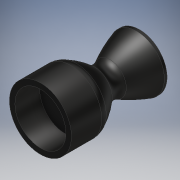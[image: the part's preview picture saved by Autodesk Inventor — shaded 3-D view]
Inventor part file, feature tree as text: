
AUTODESK INVENTOR PART (.ipt)
format: ipt  version: 2017 (Build 210142000, 142)  size: 218,624 bytes
history: native  units: mm
features: fillet x4, revolve x1, move_body x1, sketch x1
ambient origin geometry x8: Origin, YZ Plane, XZ Plane, XY Plane, X Axis, Y Axis, Z Axis, Center Point
bodies: Solid1 (feature_tree)
feature tree (7):
  revolve  "Revolution1"  [1 undecoded]
  move_body  "Move Body1"
  fillet  "Fillet6"  Radius=2.0mm
  fillet  "Fillet7"  Radius=34.965555mm
  fillet  "Fillet8"  [1 undecoded]
  fillet  "Fillet9"  Radius=2.0mm
  sketch  "Sketch1"  dims[d22=90.0deg d26=9.25mm d28=2.0mm d37=34.965555mm d38=90.0deg d51=2.0mm d52=5.0mm d53=5.0mm d54=5.0mm d57=36.0mm d59=1.0mm d60=1.0mm d61=90.0deg]
note: 2 required parameter values undecoded (feature->parameter linkage not recoverable at this tier; creation-order binding heuristic only, values carry confidence <= 0.55)